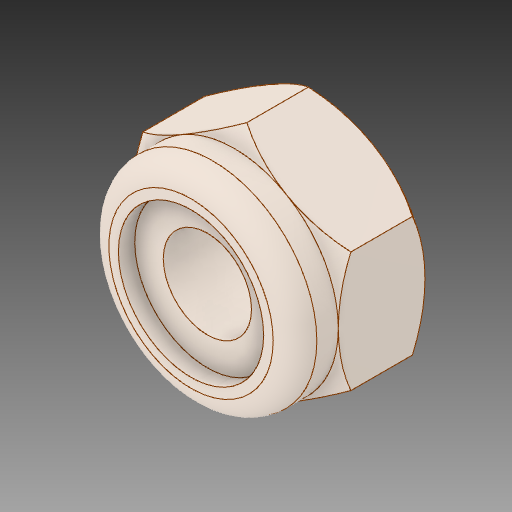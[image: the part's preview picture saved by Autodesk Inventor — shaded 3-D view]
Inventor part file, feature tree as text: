
AUTODESK INVENTOR PART (.ipt)
format: ipt  version: 2017.1 (Build 211199000, 199)  size: 173,056 bytes
history: native  units: in
note: dims shown in document units (in); Inventor stores cm internally (conversion verified against a paired STEP export)
features: fillet x1
ambient origin geometry x8: Origin, YZ Plane, XZ Plane, XY Plane, X Axis, Y Axis, Z Axis, Center Point
bodies: Solid1 (feature_tree)
feature tree (1):
  fillet  "Fillet1"  [1 undecoded]
note: 1 required parameter value undecoded (feature->parameter linkage not recoverable at this tier; creation-order binding heuristic only, values carry confidence <= 0.55)
